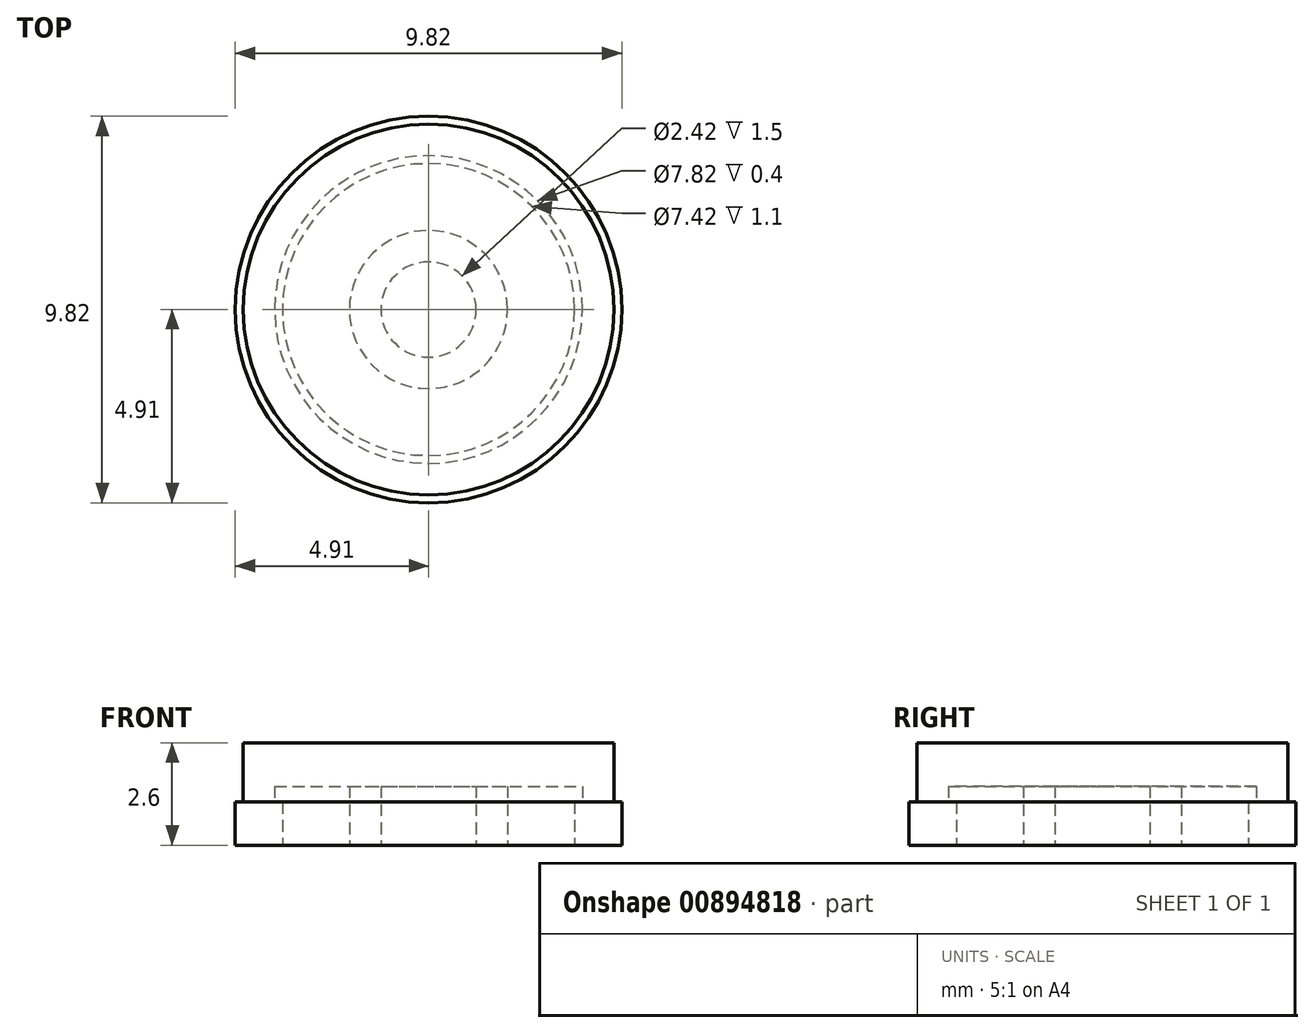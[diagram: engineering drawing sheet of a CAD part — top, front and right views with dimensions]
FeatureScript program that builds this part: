
annotation { "Feature Type Name" : "Feature", "Feature Type Description" : "" }
export const myFeature = defineFeature(function(context is Context, id is Id, definition is map)
    precondition{}
    {
        {
            var Q0;
            Q0=qCreatedBy(makeId("Front.planeOp"),FACE);
            var sketch = newSketch(context, id + "F0", { "sketchPlane" : qUnion([Q0])});
            skLineSegment(sketch, "E0.bottom", {"start": v(0, 0) * mm, "end": v(4.7, 0) * mm, "construction": true});
            skLineSegment(sketch, "E0.top", {"start": v(0, 2.6) * mm, "end": v(4.7, 2.6) * mm});
            skLineSegment(sketch, "E0.left", {"start": v(0, 0) * mm, "end": v(0, 2.6) * mm, "construction": true});
            skLineSegment(sketch, "E0.right", {"start": v(4.7, 0) * mm, "end": v(4.7, 2.6) * mm});
            skLineSegment(sketch, "E1", {"start": v(0, 2.6) * mm, "end": v(0, 1.5) * mm});
            skLineSegment(sketch, "E2", {"start": v(0, 1.5) * mm, "end": v(3.9, 1.5) * mm});
            skLineSegment(sketch, "E3", {"start": v(3.9, 1.5) * mm, "end": v(3.9, 0) * mm});
            skLineSegment(sketch, "E4", {"start": v(3.9, 0) * mm, "end": v(4.7, 0) * mm});
            skLineSegment(sketch, "E5", {"start": v(4.7, 0) * mm, "end": v(4.9, 0) * mm});
            skLineSegment(sketch, "E6", {"start": v(4.9, 0) * mm, "end": v(4.9, 1.1) * mm});
            skLineSegment(sketch, "E7", {"start": v(4.9, 1.1) * mm, "end": v(4.7, 1.1) * mm});
            skLineSegment(sketch, "E8", {"start": v(3.9, 0) * mm, "end": v(3.7, 0) * mm});
            skLineSegment(sketch, "E9", {"start": v(3.7, 0) * mm, "end": v(3.7, 1.1) * mm});
            skLineSegment(sketch, "E10", {"start": v(3.7, 1.1) * mm, "end": v(3.9, 1.1) * mm});
            skLineSegment(sketch, "E11", {"start": v(1.21, 1.5) * mm, "end": v(1.21, 0) * mm});
            skLineSegment(sketch, "E12", {"start": v(1.21, 0) * mm, "end": v(2, 0) * mm});
            skLineSegment(sketch, "E13", {"start": v(2, 0) * mm, "end": v(2, 1.5) * mm});
            skSolve(sketch);
        }
        {
            var Q0;
            {var subQ1=sQuery(id+"F0.wireOp",EDGE,"E0.top");Q0=makeQuery(id+"F0.imprint","IMPRINT",FACE,{"disambiguationData":[TD([[makeQuery(id+"F0.imprint","IMPRINT",EDGE,{"derivedFrom":subQ1}),-1.0]])]});}
            var Q1;
            {var subQ0=sQuery(id+"F0.wireOp",EDGE,"E5");Q1=makeQuery(id+"F0.imprint","IMPRINT",FACE,{"disambiguationData":[TD([[makeQuery(id+"F0.imprint","IMPRINT",EDGE,{"derivedFrom":subQ0}),1.0]])]});}
            var Q2;
            {var subQ0=sQuery(id+"F0.wireOp",EDGE,"E8");Q2=makeQuery(id+"F0.imprint","IMPRINT",FACE,{"disambiguationData":[TD([[makeQuery(id+"F0.imprint","IMPRINT",EDGE,{"derivedFrom":subQ0}),-1.0]])]});}
            var Q3;
            {var subQ0=sQuery(id+"F0.wireOp",EDGE,"3VOv9DVz-1nxT-I0Ix-l81r-0iR5ZFxI54IF");Q3=makeQuery(id+"F0.imprint","IMPRINT",FACE,{"disambiguationData":[TD([[makeQuery(id+"F0.imprint","IMPRINT",EDGE,{"derivedFrom":subQ0}),-1.0]])]});}
            var Q4;
            {var subQ0=sQuery(id+"F0.wireOp",EDGE,"8Hl1LuYG-aMcZ-5NUE-XRWw-rrl0UPWPwCj6");Q4=makeQuery(id+"F0.imprint","IMPRINT",FACE,{"disambiguationData":[TD([[makeQuery(id+"F0.imprint","IMPRINT",EDGE,{"derivedFrom":subQ0}),1.0]])]});}
            var Q5;
            {var subQ0=sQuery(id+"F0.wireOp",EDGE,"E11");Q5=makeQuery(id+"F0.imprint","IMPRINT",FACE,{"disambiguationData":[TD([[makeQuery(id+"F0.imprint","IMPRINT",EDGE,{"derivedFrom":subQ0}),1.0]])]});}
            var Q6;
            Q6=sQuery(id+"F0.wireOp",EDGE,"E0.left");
            revolve(context, id + "F1", {"surfaceOperationType" : NewSurfaceOperationType.NEW, "entities" : qUnion([Q0, Q1, Q2, Q3, Q4, Q5]), "axis" : qUnion([Q6]), "revolveType" : RevolveType.FULL});
        }
    });
